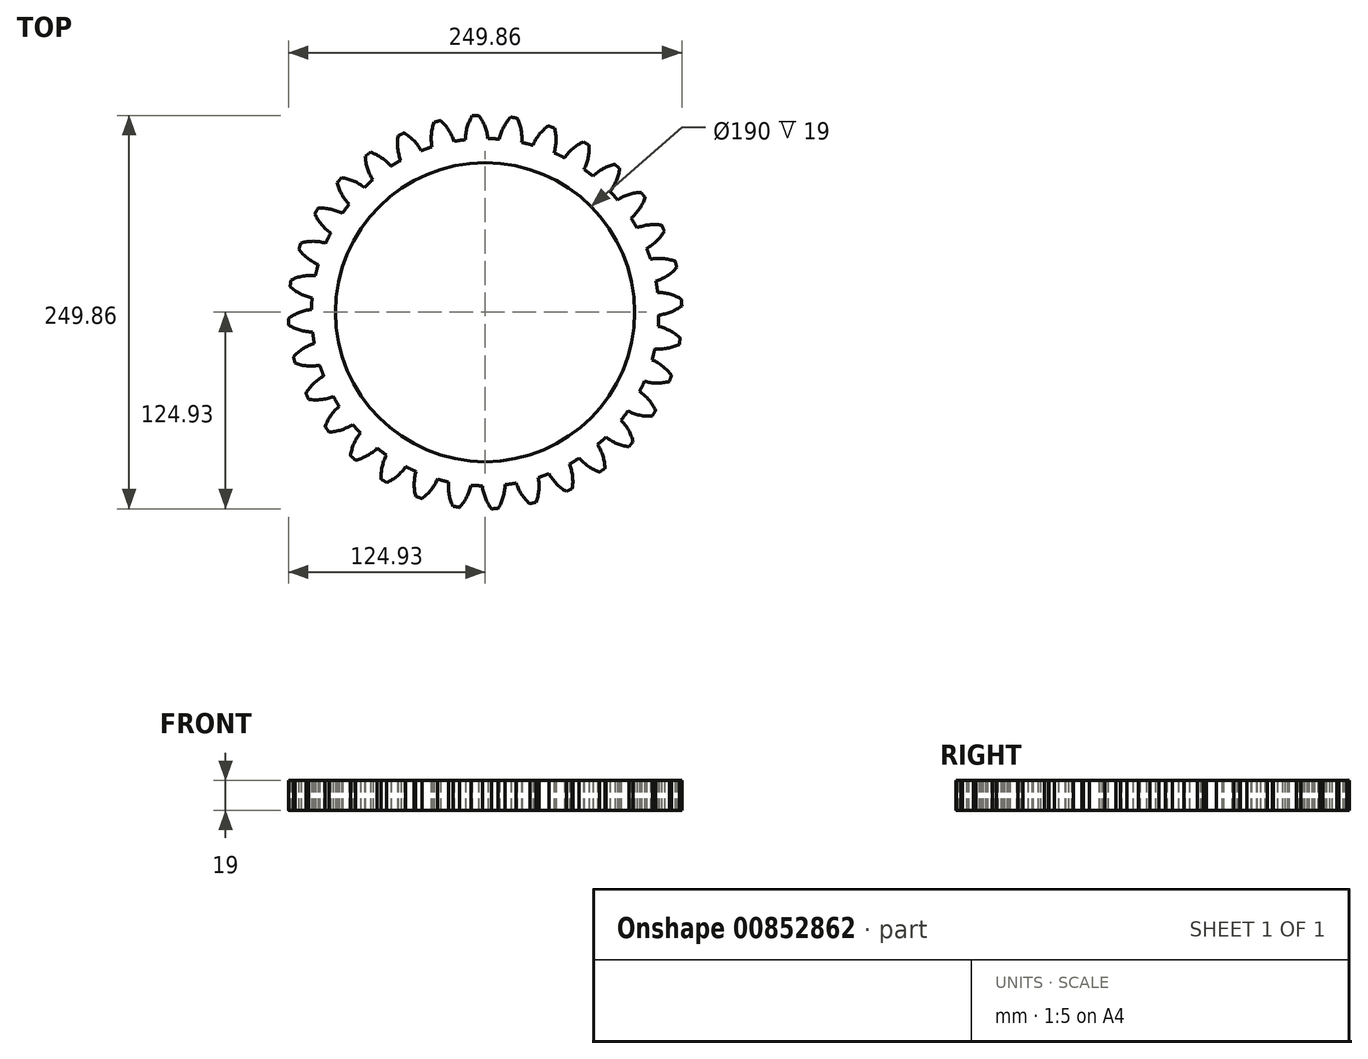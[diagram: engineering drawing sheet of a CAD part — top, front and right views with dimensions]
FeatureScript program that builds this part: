
annotation { "Feature Type Name" : "Feature", "Feature Type Description" : "" }
export const myFeature = defineFeature(function(context is Context, id is Id, definition is map)
    precondition{}
    {
        {
            var Q0;
            Q0=qCreatedBy(makeId("Top.planeOp"),FACE);
            var sketch = newSketch(context, id + "F0", { "sketchPlane" : qUnion([Q0])});
            skCircle(sketch, "E0", {"center": v(0, 0) * mm, "radius": 110.3 * mm});
            skCircle(sketch, "E1", {"center": v(0, 0) * mm, "radius": 117.64 * mm, "construction": true});
            skCircle(sketch, "E2", {"center": v(0, 0) * mm, "radius": 125 * mm, "construction": true});
            skLineSegment(sketch, "E3", {"start": v(0, 0) * mm, "end": v(0, 153.72) * mm, "construction": true});
            skLineSegment(sketch, "E4", {"start": v(0, 0) * mm, "end": v(-8.94, 181.9) * mm, "construction": true});
            skLineSegment(sketch, "E5", {"start": v(0, 117.64) * mm, "end": v(-67.78, 117.64) * mm, "construction": true});
            skLineSegment(sketch, "E6", {"start": v(0, 117.64) * mm, "end": v(-72.57, 91.23) * mm, "construction": true});
            skCircle(sketch, "E7", {"center": v(0, 117.64) * mm, "radius": 29.41 * mm, "construction": true});
            skCircle(sketch, "E8", {"center": v(0, 0) * mm, "radius": 110.55 * mm, "construction": true});
            skCircle(sketch, "E9", {"center": v(-27.45, 107.09) * mm, "radius": 29.41 * mm, "construction": true});
            skArc(sketch, "E10", {"start": v(0, 117.64) * mm, "mid": v(-1.78, 121.43) * mm, "end": v(-4.07, 124.93) * mm});
            skArc(sketch, "E11", {"start": v(1.79, 110.28) * mm, "mid": v(1.13, 114.02) * mm, "end": v(0, 117.64) * mm});
            skArc(sketch, "E12.MirrorCS", {"start": v(-11.53, 117.08) * mm, "mid": v(-10.13, 121.02) * mm, "end": v(-8.2, 124.73) * mm});
            skArc(sketch, "E13.MirrorCS", {"start": v(-12.59, 109.57) * mm, "mid": v(-12.3, 113.36) * mm, "end": v(-11.53, 117.08) * mm});
            skArc(sketch, "E14", {"start": v(-8.2, 124.73) * mm, "mid": v(-6.13, 124.8) * mm, "end": v(-4.07, 124.93) * mm});
            skCircle(sketch, "E15", {"center": v(0, 0) * mm, "radius": 95 * mm});
            skSolve(sketch);
        }
        {
            var Q0;
            {var subQ0=sQuery(id+"F0.wireOp",EDGE,"E0");var subQ1=makeQuery(id+"F0.imprint","INTERSECT",VERTEX,{"derivedFrom":[subQ0,sQuery(id+"F0.wireOp",EDGE,"E11")]});Q0=makeQuery(id+"F0.imprint","IMPRINT",FACE,{"disambiguationData":[TD([[makeQuery(id+"F0.imprint","IMPRINT",EDGE,{"disambiguationData":[TD([[subQ1,-1.0]])],"derivedFrom":subQ0}),1.0]])]});}
            var Q1;
            Q1=makeQuery(id+"F0.imprint","IMPRINT",FACE,{"disambiguationData":[TD([[makeQuery(id+"F0.imprint","IMPRINT",EDGE,{"derivedFrom":sQuery(id+"F0.wireOp",EDGE,"E10")}),1.0]])]});
            extrude(context, id + "F1", {"entities" : qUnion([Q0, Q1]), "depth" : 19 * mm, "offsetDistance" : 25 * mm});
        }
        {
            var Q0;
            Q0=makeQuery(id+"F1.opExtrude","SWEPT_BODY",BODY,{"disambiguationData":[OSD([sQuery(id+"F0.wireOp",EDGE,"E0"),sQuery(id+"F0.wireOp",EDGE,"E10"),sQuery(id+"F0.wireOp",EDGE,"E11"),sQuery(id+"F0.wireOp",EDGE,"E12.MirrorCS"),sQuery(id+"F0.wireOp",EDGE,"E13.MirrorCS"),sQuery(id+"F0.wireOp",EDGE,"E14")])]});
            var Q1;
            Q1=makeQuery(id+"F1.opExtrude","SWEPT_FACE",FACE,{"disambiguationData":[OSD([sQuery(id+"F0.wireOp",EDGE,"E0")])]});
            circularPattern(context, id + "F2", {"operationType" : NewBodyOperationType.ADD, "entities" : qUnion([Q0]), "axis" : qUnion([Q1]), "angle" : 360 * degree, "instanceCount" : 32, "equalSpace" : true});
        }
    });
